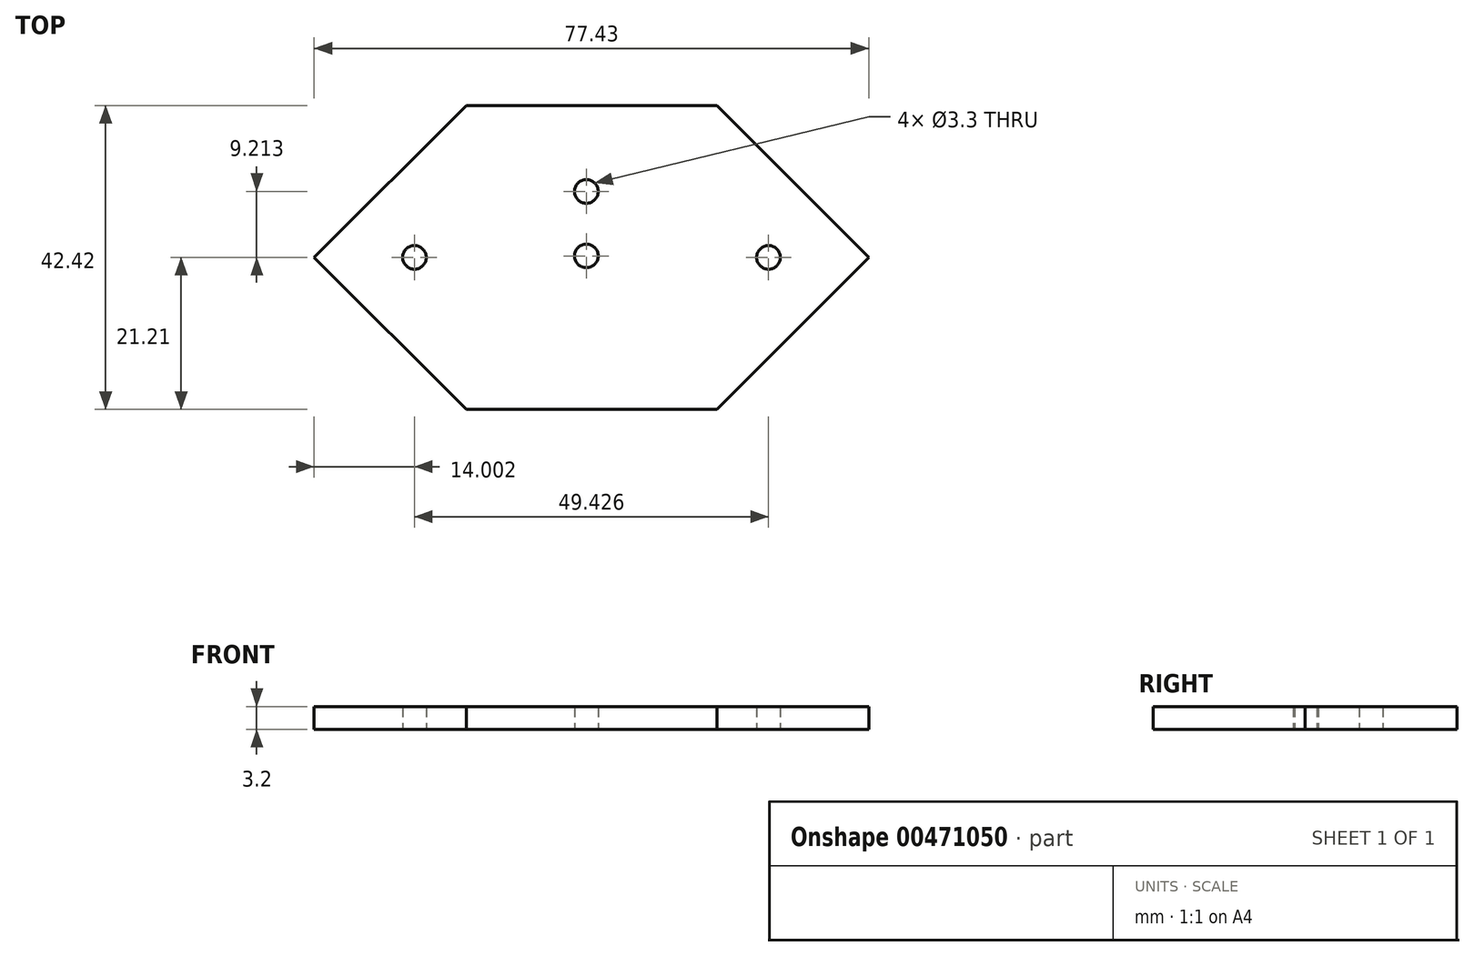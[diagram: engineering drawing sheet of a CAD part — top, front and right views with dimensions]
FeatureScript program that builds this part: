
annotation { "Feature Type Name" : "Feature", "Feature Type Description" : "" }
export const myFeature = defineFeature(function(context is Context, id is Id, definition is map)
    precondition{}
    {
        {
            var Q0;
            Q0=qCreatedBy(makeId("Top.planeOp"),FACE);
            var sketch = newSketch(context, id + "F0", { "sketchPlane" : qUnion([Q0])});
            skLineSegment(sketch, "E0", {"start": v(49.59, 0) * mm, "end": v(28.38, -21.21) * mm});
            skLineSegment(sketch, "E1", {"start": v(28.38, 21.21) * mm, "end": v(49.59, 0) * mm});
            skLineSegment(sketch, "E2", {"start": v(28.38, 21.21) * mm, "end": v(-6.62, 21.21) * mm});
            skLineSegment(sketch, "E3", {"start": v(-6.62, -21.21) * mm, "end": v(28.38, -21.21) * mm});
            skLineSegment(sketch, "E4", {"start": v(-6.62, 21.21) * mm, "end": v(-27.84, 0) * mm});
            skLineSegment(sketch, "E5", {"start": v(-27.84, 0) * mm, "end": v(-6.62, -21.21) * mm});
            skLineSegment(sketch, "E6", {"start": v(-27.84, 0) * mm, "end": v(49.59, 0) * mm});
            skCircle(sketch, "E7", {"center": v(-13.84, 0) * mm, "radius": 1.65 * mm});
            skCircle(sketch, "E8", {"center": v(35.59, 0) * mm, "radius": 1.65 * mm});
            skCircle(sketch, "E9", {"center": v(10.16, 9.21) * mm, "radius": 1.65 * mm});
            skCircle(sketch, "E10", {"center": v(10.16, 0.21) * mm, "radius": 1.65 * mm});
            skSolve(sketch);
        }
        {
            var Q0;
            Q0 = qSketchRegion(id + "F0", true);
            extrude(context, id + "F1", {"entities" : qUnion([Q0]), "depth" : 3.2 * mm, "offsetDistance" : 25 * mm});
        }
    });
